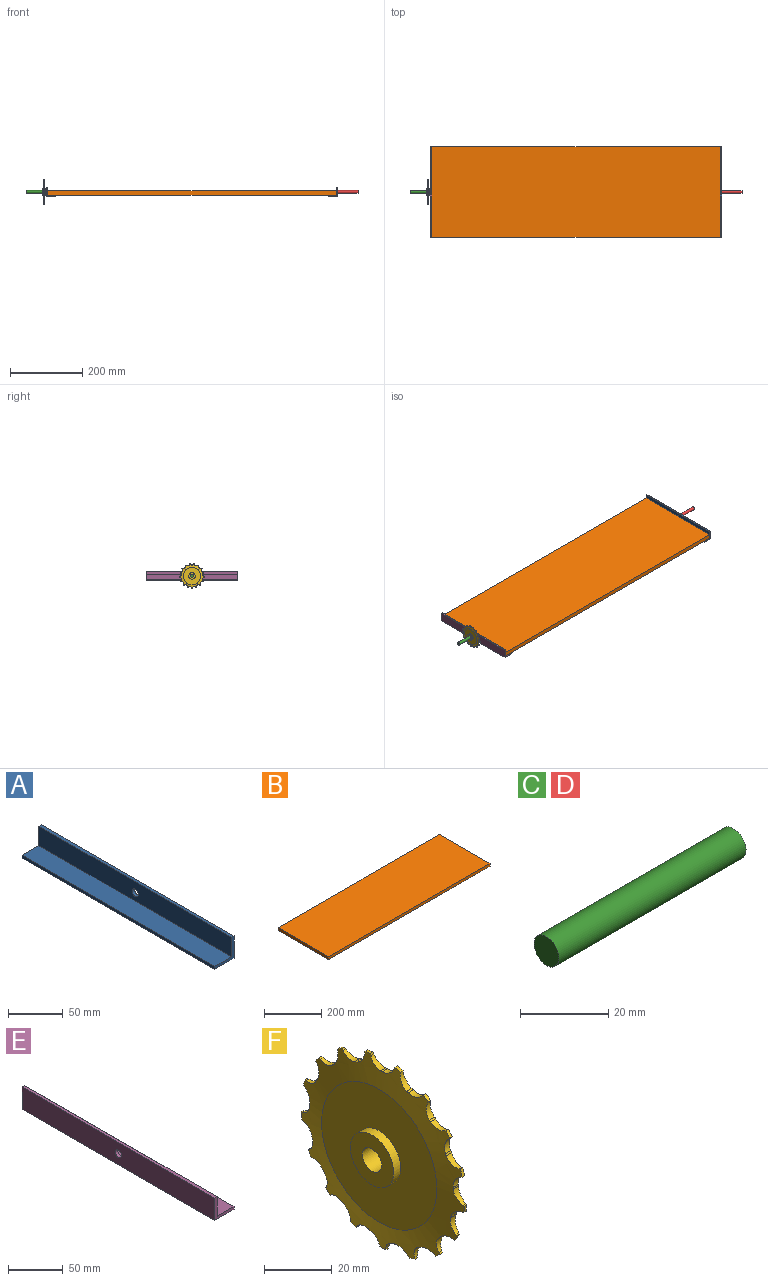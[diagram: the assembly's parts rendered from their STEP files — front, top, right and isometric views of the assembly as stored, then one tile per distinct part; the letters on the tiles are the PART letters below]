
ASSEMBLY  parts=6 mates=5
PART A: 9 faces, bbox 25x250x25 mm
  f0: plane 250x25mm, normal (0,0,-1), area 6250mm2, adj f1,f5,f6,f7
  f1: plane 250x25mm, normal (1,0,0), area 6199.7mm2, adj f0,f2,f6,f7,f8
  f2: plane 250x3.2mm, normal (0,0,1), area 800mm2, adj f1,f3,f6,f7
  f3: plane 250x21.8mm, normal (-1,0,0), area 5399.7mm2, adj f2,f4,f6,f7,f8
  f4: plane 250x21.8mm, normal (0,0,1), area 5450mm2, adj f3,f5,f6,f7
  f5: plane 250x3.2mm, normal (-1,0,0), area 800mm2, adj f0,f4,f6,f7
  f6: plane 25x25mm, normal (0,-1,0), area 149.8mm2, adj f0,f1,f2,f3,f4,f5
  f7: plane 25x25mm, normal (0,1,0), area 149.8mm2, adj f0,f1,f2,f3,f4,f5
  f8: cylinder r=4mm len=8mm, axis (1,0,0), area 80.4mm2, adj f1,f3
PART B: 6 faces, bbox 800x250x12 mm
  f0: plane 800x12mm, normal (0,1,0), area 9600mm2, adj f1,f3,f4,f5
  f1: plane 250x12mm, normal (-1,0,0), area 3000mm2, adj f0,f2,f4,f5
  f2: plane 800x12mm, normal (0,-1,0), area 9600mm2, adj f1,f3,f4,f5
  f3: plane 250x12mm, normal (1,0,0), area 3000mm2, adj f0,f2,f4,f5
  f4: plane 800x250mm, normal (0,0,1), area 200000mm2, adj f0,f1,f2,f3
  f5: plane 800x250mm, normal (0,0,-1), area 200000mm2, adj f0,f1,f2,f3
PART C: 3 faces, bbox 60x8x8 mm
  f0: cylinder r=4mm len=60mm, axis (-1,0,0), area 1508mm2, adj f1,f2
  f1: plane 8x8mm, normal (1,0,0), area 50.3mm2, adj f0
  f2: plane 8x8mm, normal (-1,0,0), area 50.3mm2, adj f0
PART D: same geometry as C
PART E: 11 faces, bbox 25x250x25 mm
  f0: plane 250x21.8mm, normal (0,0,1), area 5410.7mm2, adj f1,f5,f6,f7,f9,f10
  f1: plane 250x21.8mm, normal (1,0,0), area 5399.7mm2, adj f0,f2,f6,f7,f8
  f2: plane 250x3.2mm, normal (0,0,1), area 800mm2, adj f1,f3,f6,f7
  f3: plane 250x25mm, normal (-1,0,0), area 6199.7mm2, adj f2,f4,f6,f7,f8
  f4: plane 250x25mm, normal (0,0,-1), area 6210.7mm2, adj f3,f5,f6,f7,f9,f10
  f5: plane 250x3.2mm, normal (1,0,0), area 800mm2, adj f0,f4,f6,f7
  f6: plane 25x25mm, normal (0,-1,0), area 149.8mm2, adj f0,f1,f2,f3,f4,f5
  f7: plane 25x25mm, normal (0,1,0), area 149.8mm2, adj f0,f1,f2,f3,f4,f5
  f8: cylinder r=4mm len=8mm, axis (1,0,0), area 80.4mm2, adj f1,f3
  f9: cylinder r=2.5mm len=5mm, axis (0,0,1), area 50.3mm2, adj f0,f4
  f10: cylinder r=2.5mm len=5mm, axis (0,0,1), area 50.3mm2, adj f0,f4
PART F: 111 faces, bbox 10x68x68 mm
  f0: cylinder r=34mm len=2.49mm, axis (1,0,0), area 2.5mm2, adj f1,f97,f98,f110
  f1: plane 1.16x0.54mm, normal (0,1,-0.02), area 0.6mm2, adj f0,f2,f97,f98
  f2: cylinder r=4.75mm len=4.54mm, axis (1,0,0), area 10.7mm2, adj f1,f3,f97,f98
  f3: cylinder r=30mm len=2.2mm, axis (1,0,0), area 1.3mm2, adj f2,f4,f97,f98
  f4: cylinder r=4.75mm len=5.34mm, axis (1,0,0), area 10.7mm2, adj f3,f5,f97,f98
  f5: plane 1.16x0.41mm, normal (0,-0.75,0.66), area 0.6mm2, adj f4,f6,f97,f98
  f6: cylinder r=34mm len=2.15mm, axis (1,0,0), area 2.5mm2, adj f5,f7,f97,f98
  f7: plane 1.16x0.5mm, normal (0,0.92,-0.38), area 0.6mm2, adj f6,f8,f97,f98
  f8: cylinder r=4.75mm len=5.35mm, axis (1,0,0), area 10.7mm2, adj f7,f9,f97,f98
  f9: cylinder r=30mm len=2.2mm, axis (1,0,0), area 1.3mm2, adj f8,f10,f97,f98
  f10: cylinder r=4.75mm len=5.44mm, axis (1,0,0), area 10.7mm2, adj f9,f11,f97,f98
  f11: plane 1.16x0.48mm, normal (0,-0.46,0.89), area 0.6mm2, adj f10,f12,f97,f98
  f12: cylinder r=34mm len=2.02mm, axis (1,0,0), area 2.5mm2, adj f11,f13,f97,f98
  f13: plane 1.16x0.39mm, normal (0,0.73,-0.69), area 0.6mm2, adj f12,f14,f97,f98
  f14: cylinder r=4.75mm len=5.43mm, axis (1,0,0), area 10.7mm2, adj f13,f15,f97,f98
  f15: cylinder r=30mm len=2.2mm, axis (1,0,0), area 1.3mm2, adj f14,f16,f97,f98
  f16: cylinder r=4.75mm len=4.81mm, axis (1,0,0), area 10.7mm2, adj f15,f17,f97,f98
  f17: plane 1.16x0.54mm, normal (0,-0.11,0.99), area 0.6mm2, adj f16,f18,f97,f98
  f18: cylinder r=34mm len=2.43mm, axis (1,0,0), area 2.5mm2, adj f17,f19,f97,f98
  f19: plane 1.16x0.49mm, normal (0,0.43,-0.9), area 0.6mm2, adj f18,f20,f97,f98
  f20: cylinder r=4.75mm len=4.78mm, axis (1,0,0), area 10.7mm2, adj f19,f21,f97,f98
  f21: cylinder r=30mm len=2.2mm, axis (1,0,0), area 1.3mm2, adj f20,f22,f97,f98
  f22: cylinder r=4.75mm len=4.2mm, axis (1,0,0), area 10.7mm2, adj f21,f23,f97,f98
  f23: plane 1.16x0.52mm, normal (0,0.25,0.97), area 0.6mm2, adj f22,f24,f97,f98
  f24: cylinder r=34mm len=2.52mm, axis (1,0,0), area 2.5mm2, adj f23,f25,f97,f98
  f25: plane 1.16x0.54mm, normal (0,0.07,-1), area 0.6mm2, adj f24,f26,f97,f98
  f26: cylinder r=4.75mm len=4.24mm, axis (1,0,0), area 10.7mm2, adj f25,f27,f97,f98
  f27: cylinder r=30mm len=2.2mm, axis (1,0,0), area 1.3mm2, adj f26,f28,f97,f98
  f28: cylinder r=4.75mm len=5.19mm, axis (1,0,0), area 10.7mm2, adj f27,f29,f97,f98
  f29: plane 1.16x0.44mm, normal (0,0.59,0.81), area 0.6mm2, adj f28,f30,f97,f98
  f30: cylinder r=34mm len=2.26mm, axis (1,0,0), area 2.5mm2, adj f29,f31,f97,f98
  f31: plane 1.16x0.52mm, normal (0,-0.29,-0.96), area 0.6mm2, adj f30,f32,f97,f98
  f32: cylinder r=4.75mm len=5.21mm, axis (1,0,0), area 10.7mm2, adj f31,f33,f97,f98
  f33: cylinder r=30mm len=2.2mm, axis (1,0,0), area 1.3mm2, adj f32,f34,f97,f98
  f34: cylinder r=4.75mm len=5.48mm, axis (1,0,0), area 10.7mm2, adj f33,f35,f97,f98
  f35: plane 1.16x0.45mm, normal (0,0.84,0.54), area 0.6mm2, adj f34,f36,f97,f98
  f36: cylinder r=34mm len=1.87mm, axis (1,0,0), area 2.5mm2, adj f35,f37,f97,f98
  f37: plane 1.16x0.42mm, normal (0,-0.62,-0.79), area 0.6mm2, adj f36,f38,f97,f98
  f38: cylinder r=4.75mm len=5.48mm, axis (1,0,0), area 10.7mm2, adj f37,f39,f97,f98
  f39: cylinder r=30mm len=2.2mm, axis (1,0,0), area 1.3mm2, adj f38,f40,f97,f98
  f40: cylinder r=4.75mm len=5.03mm, axis (1,0,0), area 10.7mm2, adj f39,f41,f97,f98
  f41: plane 1.16x0.53mm, normal (0,0.98,0.2), area 0.6mm2, adj f40,f42,f97,f98
  f42: cylinder r=34mm len=2.36mm, axis (1,0,0), area 2.5mm2, adj f41,f43,f97,f98
  f43: plane 1.16x0.47mm, normal (0,-0.86,-0.51), area 0.6mm2, adj f42,f44,f97,f98
  f44: cylinder r=4.75mm len=5.01mm, axis (1,0,0), area 10.7mm2, adj f43,f45,f97,f98
  f45: cylinder r=30mm len=2.2mm, axis (1,0,0), area 1.3mm2, adj f44,f46,f97,f98
  f46: cylinder r=4.75mm len=3.9mm, axis (1,0,0), area 10.7mm2, adj f45,f47,f97,f98
  f47: plane 1.16x0.53mm, normal (0,0.99,-0.16), area 0.6mm2, adj f46,f48,f97,f98
  f48: cylinder r=34mm len=2.53mm, axis (1,0,0), area 2.5mm2, adj f47,f49,f97,f98
  f49: plane 1.16x0.53mm, normal (0,-0.99,-0.16), area 0.6mm2, adj f48,f50,f97,f98
  f50: cylinder r=4.75mm len=3.9mm, axis (1,0,0), area 10.7mm2, adj f49,f51,f97,f98
  f51: cylinder r=30mm len=2.2mm, axis (1,0,0), area 1.3mm2, adj f50,f52,f97,f98
  f52: cylinder r=4.75mm len=5.01mm, axis (1,0,0), area 10.7mm2, adj f51,f53,f97,f98
  f53: plane 1.16x0.47mm, normal (0,0.86,-0.51), area 0.6mm2, adj f52,f54,f97,f98
  f54: cylinder r=34mm len=2.36mm, axis (1,0,0), area 2.5mm2, adj f53,f55,f97,f98
  f55: plane 1.16x0.53mm, normal (0,-0.98,0.2), area 0.6mm2, adj f54,f56,f97,f98
  f56: cylinder r=4.75mm len=5.03mm, axis (1,0,0), area 10.7mm2, adj f55,f57,f97,f98
  f57: cylinder r=30mm len=2.2mm, axis (1,0,0), area 1.3mm2, adj f56,f58,f97,f98
  f58: cylinder r=4.75mm len=5.48mm, axis (1,0,0), area 10.7mm2, adj f57,f59,f97,f98
  f59: plane 1.16x0.42mm, normal (0,0.62,-0.79), area 0.6mm2, adj f58,f60,f97,f98
  f60: cylinder r=34mm len=1.87mm, axis (1,0,0), area 2.5mm2, adj f59,f61,f97,f98
  f61: plane 1.16x0.45mm, normal (0,-0.84,0.54), area 0.6mm2, adj f60,f62,f97,f98
  f62: cylinder r=4.75mm len=5.48mm, axis (1,0,0), area 10.7mm2, adj f61,f63,f97,f98
  f63: cylinder r=30mm len=2.2mm, axis (1,0,0), area 1.3mm2, adj f62,f64,f97,f98
  f64: cylinder r=4.75mm len=5.21mm, axis (1,0,0), area 10.7mm2, adj f63,f65,f97,f98
  f65: plane 1.16x0.52mm, normal (0,0.29,-0.96), area 0.6mm2, adj f64,f66,f97,f98
  f66: cylinder r=34mm len=2.26mm, axis (1,0,0), area 2.5mm2, adj f65,f67,f97,f98
  f67: plane 1.16x0.44mm, normal (0,-0.59,0.81), area 0.6mm2, adj f66,f68,f97,f98
  f68: cylinder r=4.75mm len=5.19mm, axis (1,0,0), area 10.7mm2, adj f67,f69,f97,f98
  f69: cylinder r=30mm len=2.2mm, axis (1,0,0), area 1.3mm2, adj f68,f70,f97,f98
  f70: cylinder r=4.75mm len=4.24mm, axis (1,0,0), area 10.7mm2, adj f69,f71,f97,f98
  f71: plane 1.16x0.54mm, normal (0,-0.07,-1), area 0.6mm2, adj f70,f72,f97,f98
  f72: cylinder r=34mm len=2.52mm, axis (1,0,0), area 2.5mm2, adj f71,f73,f97,f98
  f73: plane 1.16x0.52mm, normal (0,-0.25,0.97), area 0.6mm2, adj f72,f74,f97,f98
  f74: cylinder r=4.75mm len=4.2mm, axis (1,0,0), area 10.7mm2, adj f73,f75,f97,f98
  f75: cylinder r=30mm len=2.2mm, axis (1,0,0), area 1.3mm2, adj f74,f76,f97,f98
  f76: cylinder r=4.75mm len=4.78mm, axis (1,0,0), area 10.7mm2, adj f75,f77,f97,f98
  f77: plane 1.16x0.49mm, normal (0,-0.43,-0.9), area 0.6mm2, adj f76,f78,f97,f98
  f78: cylinder r=34mm len=2.43mm, axis (1,0,0), area 2.5mm2, adj f77,f79,f97,f98
  f79: plane 1.16x0.54mm, normal (0,0.11,0.99), area 0.6mm2, adj f78,f80,f97,f98
  f80: cylinder r=4.75mm len=4.81mm, axis (1,0,0), area 10.7mm2, adj f79,f81,f97,f98
  f81: cylinder r=30mm len=2.2mm, axis (1,0,0), area 1.3mm2, adj f80,f82,f97,f98
  f82: cylinder r=4.75mm len=5.43mm, axis (1,0,0), area 10.7mm2, adj f81,f83,f97,f98
  f83: plane 1.16x0.39mm, normal (0,-0.73,-0.69), area 0.6mm2, adj f82,f84,f97,f98
  f84: cylinder r=34mm len=2.02mm, axis (1,0,0), area 2.5mm2, adj f83,f85,f97,f98
  f85: plane 1.16x0.48mm, normal (0,0.46,0.89), area 0.6mm2, adj f84,f86,f97,f98
  f86: cylinder r=4.75mm len=5.44mm, axis (1,0,0), area 10.7mm2, adj f85,f87,f97,f98
  f87: cylinder r=30mm len=2.2mm, axis (1,0,0), area 1.3mm2, adj f86,f88,f97,f98
  f88: cylinder r=4.75mm len=5.35mm, axis (1,0,0), area 10.7mm2, adj f87,f89,f97,f98
  f89: plane 1.16x0.5mm, normal (0,-0.92,-0.38), area 0.6mm2, adj f88,f90,f97,f98
  f90: cylinder r=34mm len=2.15mm, axis (1,0,0), area 2.5mm2, adj f89,f91,f97,f98
  f91: plane 1.16x0.41mm, normal (0,0.75,0.66), area 0.6mm2, adj f90,f92,f97,f98
  f92: cylinder r=4.75mm len=5.34mm, axis (1,0,0), area 10.7mm2, adj f91,f93,f97,f98
  f93: cylinder r=30mm len=2.2mm, axis (1,0,0), area 1.3mm2, adj f92,f94,f97,f98
  f94: cylinder r=4.75mm len=4.54mm, axis (1,0,0), area 10.7mm2, adj f93,f95,f97,f98
  f95: plane 1.16x0.54mm, normal (0,-1,-0.02), area 0.6mm2, adj f94,f96,f97,f98
  f96: cylinder r=34mm len=2.49mm, axis (1,0,0), area 2.5mm2, adj f95,f97,f98,f106
  f97: cone r=24mm half-angle=81.5deg, axis (-1,0,0), area 1327.6mm2, adj f0,f1,f2,f3,f4,f5,f6,f7
  f98: cone r=24mm half-angle=81.5deg, axis (1,0,0), area 1327.6mm2, adj f0,f1,f2,f3,f4,f5,f6,f7
  f99: cylinder r=4mm len=10mm, axis (1,0,0), area 251.3mm2, adj f100,f105
  f100: plane 18x18mm, normal (1,0,0), area 204.2mm2, adj f99,f101
  f101: cylinder r=9mm len=18mm, axis (1,0,0), area 169.6mm2, adj f100,f102
  f102: plane 48x48mm, normal (1,0,0), area 1555.1mm2, adj f97,f101
  f103: plane 48x48mm, normal (-1,0,0), area 1555.1mm2, adj f98,f104
  f104: cylinder r=9mm len=18mm, axis (1,0,0), area 169.6mm2, adj f103,f105
  f105: plane 18x18mm, normal (-1,0,0), area 204.2mm2, adj f99,f104
  f106: plane 1.16x0.51mm, normal (0,0.94,0.34), area 0.6mm2, adj f96,f97,f98,f107
  f107: cylinder r=4.75mm len=4.51mm, axis (1,0,0), area 10.7mm2, adj f97,f98,f106,f108
  f108: cylinder r=30mm len=2.2mm, axis (1,0,0), area 1.3mm2, adj f97,f98,f107,f109
  f109: cylinder r=4.75mm len=4.51mm, axis (1,0,0), area 10.7mm2, adj f97,f98,f108,f110
  f110: plane 1.16x0.51mm, normal (0,-0.94,0.34), area 0.6mm2, adj f0,f97,f98,f109
PLACE A t=(397.68,-2.33,-8.01)mm
PLACE B t=(-5.52,-2.33,1.29)mm
PLACE C t=(-435.52,-2.33,4.49)mm
PLACE D t=(424.48,-2.33,4.49)mm
PLACE E t=(-405.52,-2.33,-4.81)mm
PLACE F t=(-415.52,-2.33,4.49)mm
MATE fastened C.f0 <-> B.f1  axis (1,0,0) through (-405.52,-2.33,4.49)mm
MATE fastened D.f0 <-> A.f8  axis (-1,0,0) through (394.48,-2.33,4.49)mm
MATE fastened D.f0 <-> B.f3  axis (-1,0,0) through (394.48,-2.33,4.49)mm
MATE fastened F.f0 <-> C.f0  axis (1,0,0) through (-410.52,-2.33,4.49)mm
MATE fastened C.f0 <-> E.f8  axis (-1,0,0) through (-405.52,-2.33,4.49)mm
